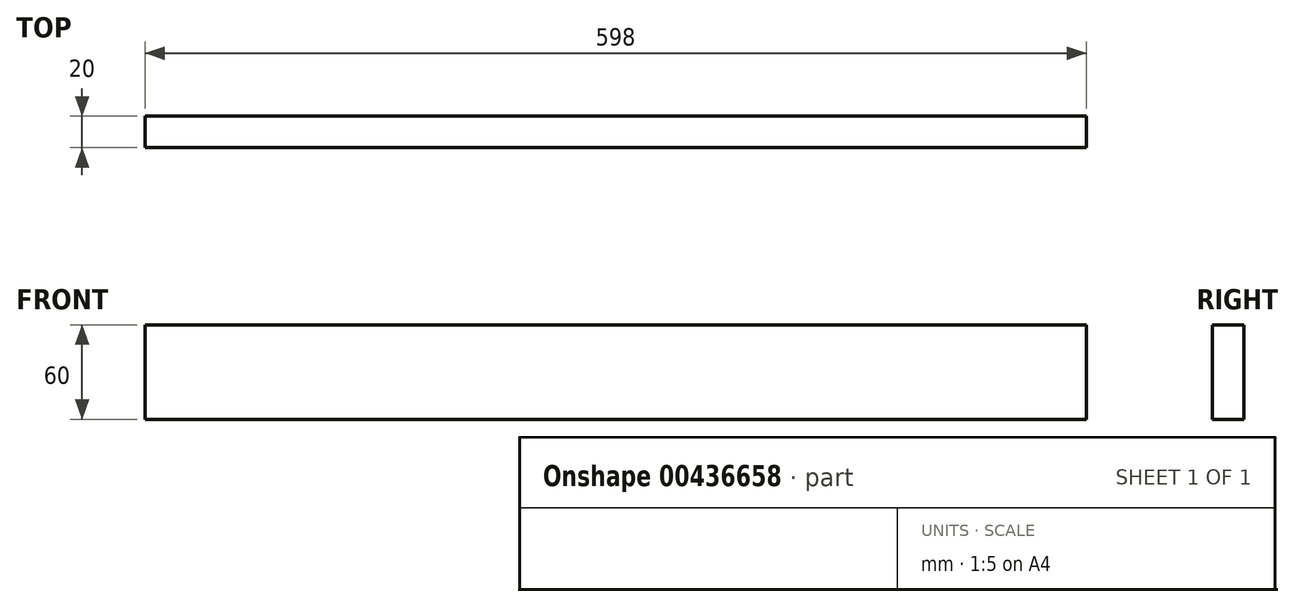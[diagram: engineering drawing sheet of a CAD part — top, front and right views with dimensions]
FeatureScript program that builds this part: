
annotation { "Feature Type Name" : "Feature", "Feature Type Description" : "" }
export const myFeature = defineFeature(function(context is Context, id is Id, definition is map)
    precondition{}
    {
        {
            var Q0;
            Q0=qCreatedBy(makeId("Right.planeOp"),FACE);
            var sketch = newSketch(context, id + "F0", { "sketchPlane" : qUnion([Q0])});
            skLineSegment(sketch, "E0.bottom", {"start": v(10, -30) * mm, "end": v(-10, -30) * mm});
            skLineSegment(sketch, "E0.top", {"start": v(10, 30) * mm, "end": v(-10, 30) * mm});
            skLineSegment(sketch, "E0.left", {"start": v(10, -30) * mm, "end": v(10, 30) * mm});
            skLineSegment(sketch, "E0.right", {"start": v(-10, -30) * mm, "end": v(-10, 30) * mm});
            skPoint(sketch, "E0.middle", {"position": v(0, 0) * mm});
            skSolve(sketch);
        }
        {
            var Q0;
            Q0=qSketchRegion(id+"F0",true);
            extrude(context, id + "F1", {"entities" : qUnion([Q0]), "depth" : 598 * mm});
        }
    });
